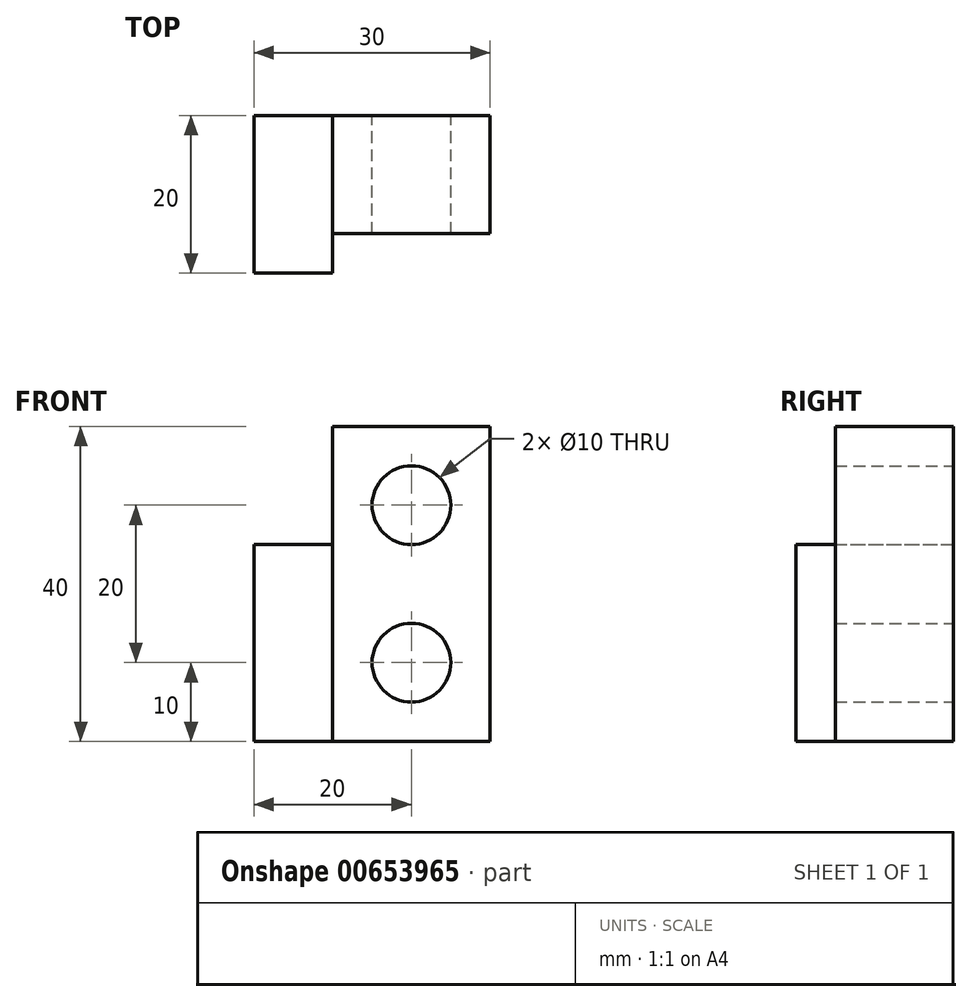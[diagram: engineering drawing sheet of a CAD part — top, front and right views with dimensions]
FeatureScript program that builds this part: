
annotation { "Feature Type Name" : "Feature", "Feature Type Description" : "" }
export const myFeature = defineFeature(function(context is Context, id is Id, definition is map)
    precondition{}
    {
        {
            var Q0;
            Q0=qCreatedBy(makeId("Front.planeOp"),FACE);
            var sketch = newSketch(context, id + "F0", { "sketchPlane" : qUnion([Q0])});
            skLineSegment(sketch, "E0.bottom", {"start": v(10, -20) * mm, "end": v(-10, -20) * mm});
            skLineSegment(sketch, "E0.top", {"start": v(10, 20) * mm, "end": v(-10, 20) * mm});
            skLineSegment(sketch, "E0.left", {"start": v(10, -20) * mm, "end": v(10, 20) * mm});
            skLineSegment(sketch, "E0.right", {"start": v(-10, -20) * mm, "end": v(-10, 20) * mm});
            skPoint(sketch, "E0.middle", {"position": v(0, 0) * mm});
            skLineSegment(sketch, "E1.bottom", {"start": v(-10, -20) * mm, "end": v(-20, -20) * mm});
            skLineSegment(sketch, "E1.top", {"start": v(-10, 5) * mm, "end": v(-20, 5) * mm});
            skLineSegment(sketch, "E1.left", {"start": v(-10, -20) * mm, "end": v(-10, 5) * mm});
            skLineSegment(sketch, "E1.right", {"start": v(-20, -20) * mm, "end": v(-20, 5) * mm});
            skCircle(sketch, "E2", {"center": v(0, -10) * mm, "radius": 5 * mm});
            skSolve(sketch);
        }
        {
            var Q0;
            Q0=makeQuery(id+"F0.imprint","IMPRINT",FACE,{"disambiguationData":[TD([[makeQuery(id+"F0.imprint","IMPRINT",EDGE,{"derivedFrom":sQuery(id+"F0.wireOp",EDGE,"E0.bottom")}),-1.0]])]});
            extrude(context, id + "F1", {"entities" : qUnion([Q0]), "depth" : 15 * mm, "offsetDistance" : 25 * mm});
        }
        {
            var Q0;
            Q0=makeQuery(id+"F0.imprint","IMPRINT",FACE,{"disambiguationData":[TD([[makeQuery(id+"F0.imprint","IMPRINT",EDGE,{"derivedFrom":sQuery(id+"F0.wireOp",EDGE,"E1.bottom")}),-1.0]])]});
            extrude(context, id + "F2", {"entities" : qUnion([Q0]), "operationType" : NewBodyOperationType.ADD, "depth" : 20 * mm, "offsetDistance" : 25 * mm});
        }
        {
            var Q0;
            Q0=qCreatedBy(makeId("Front.planeOp"),FACE);
            var sketch = newSketch(context, id + "F3", { "sketchPlane" : qUnion([Q0])});
            skCircle(sketch, "E3", {"center": v(0, 10) * mm, "radius": 5 * mm});
            skSolve(sketch);
        }
        {
            var Q0;
            Q0 = qSketchRegion(id + "F3", true);
            var Q1;
            Q1=makeQuery(id+"F1.opExtrude","CAP_FACE",FACE,{"disambiguationData":[OSD([sQuery(id+"F0.wireOp",EDGE,"E0.bottom"),sQuery(id+"F0.wireOp",EDGE,"E0.top"),sQuery(id+"F0.wireOp",EDGE,"E0.left"),sQuery(id+"F0.wireOp",EDGE,"E0.right"),sQuery(id+"F0.wireOp",EDGE,"E1.left"),sQuery(id+"F0.wireOp",EDGE,"E2")])],"isStart":false});
            extrude(context, id + "F4", {"entities" : qUnion([Q0]), "operationType" : NewBodyOperationType.REMOVE, "endBound" : BoundingType.UP_TO_SURFACE, "depth" : 25 * mm, "endBoundEntityFace" : qUnion([Q1]), "offsetDistance" : 25 * mm});
        }
    });
